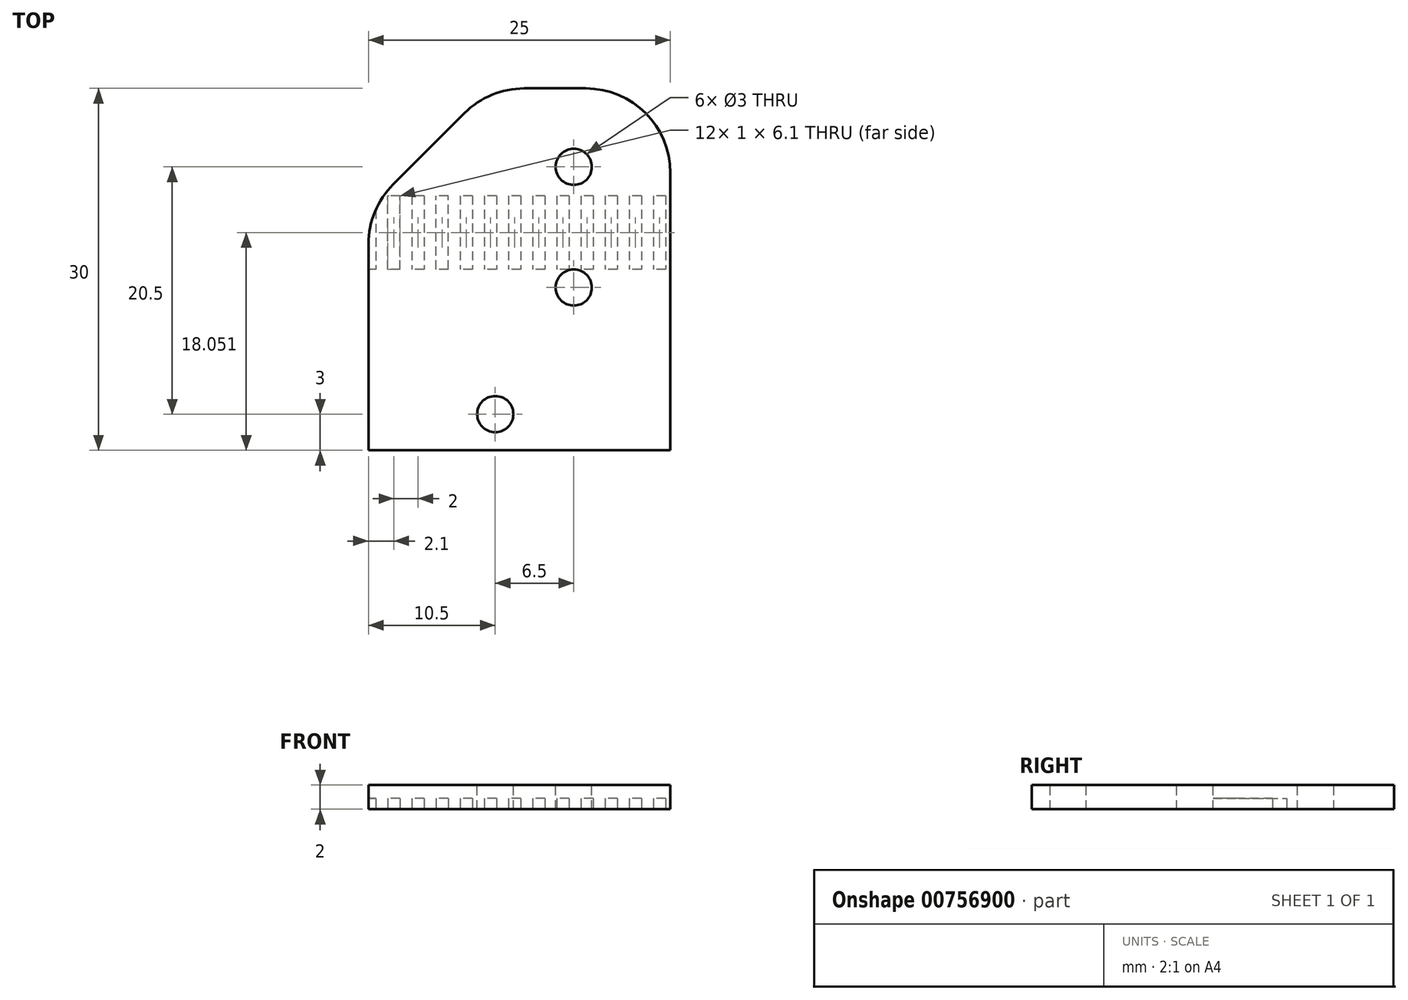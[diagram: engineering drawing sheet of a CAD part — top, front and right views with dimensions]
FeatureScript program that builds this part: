
annotation { "Feature Type Name" : "Feature", "Feature Type Description" : "" }
export const myFeature = defineFeature(function(context is Context, id is Id, definition is map)
    precondition{}
    {
        {
            var Q0;
            Q0=qCreatedBy(makeId("Top.planeOp"),FACE);
            var sketch = newSketch(context, id + "F0", { "sketchPlane" : qUnion([Q0])});
            skLineSegment(sketch, "E0.bottom", {"start": v(12.5, -15) * mm, "end": v(-12.5, -15) * mm});
            skLineSegment(sketch, "E0.top", {"start": v(12.5, 15) * mm, "end": v(-12.5, 15) * mm});
            skLineSegment(sketch, "E0.left", {"start": v(12.5, -15) * mm, "end": v(12.5, 15) * mm});
            skLineSegment(sketch, "E0.right", {"start": v(-12.5, -15) * mm, "end": v(-12.5, 15) * mm});
            skPoint(sketch, "E0.middle", {"position": v(0, 0) * mm});
            skSolve(sketch);
        }
        {
            var Q0;
            Q0=makeQuery(id+"F0.imprint","IMPRINT",FACE,{"disambiguationData":[TD([[makeQuery(id+"F0.imprint","IMPRINT",EDGE,{"derivedFrom":sQuery(id+"F0.wireOp",EDGE,"E0.bottom")}),-1.0]])]});
            extrude(context, id + "F1", {"entities" : qUnion([Q0]), "depth" : 2 * mm, "offsetDistance" : 25 * mm});
        }
        {
            var Q0;
            Q0=makeQuery(id+"F1.opExtrude","CAP_FACE",FACE,{"disambiguationData":[OSD([sQuery(id+"F0.wireOp",EDGE,"E0.bottom"),sQuery(id+"F0.wireOp",EDGE,"E0.top"),sQuery(id+"F0.wireOp",EDGE,"E0.left"),sQuery(id+"F0.wireOp",EDGE,"E0.right")])],"isStart":false});
            var sketch = newSketch(context, id + "F2", { "sketchPlane" : qUnion([Q0])});
            skCircle(sketch, "E1", {"center": v(-2, -12) * mm, "radius": 1.5 * mm});
            skPoint(sketch, "E1.centerSnap0", {"position": v(0, -15) * mm});
            skCircle(sketch, "E2", {"center": v(4.5, -1.5) * mm, "radius": 1.5 * mm});
            skCircle(sketch, "E3", {"center": v(4.5, 8.5) * mm, "radius": 1.5 * mm});
            skSolve(sketch);
        }
        {
            var Q0;
            Q0=qSketchRegion(id+"F2",true);
            extrude(context, id + "F3", {"entities" : qUnion([Q0]), "operationType" : NewBodyOperationType.REMOVE, "endBound" : BoundingType.THROUGH_ALL, "oppositeDirection" : true, "depth" : 25 * mm, "offsetDistance" : 25 * mm});
        }
        {
            var Q0;
            {var subQ0=sQuery(id+"F0.wireOp",EDGE,"E0.right");var subQ1=sQuery(id+"F0.wireOp",EDGE,"E0.left");var subQ2=sQuery(id+"F0.wireOp",EDGE,"E0.bottom");Q0=makeQuery(id+"F5.boolean.opBoolean","SPLIT",FACE,{"disambiguationData":[TD([makeQuery(id+"F1.opExtrude","SWEPT_FACE",FACE,{"disambiguationData":[OSD([subQ2])]})])],"derivedFrom":makeQuery(id+"F1.opExtrude","CAP_FACE",FACE,{"disambiguationData":[OSD([subQ2,sQuery(id+"F0.wireOp",EDGE,"E0.top"),subQ1,subQ0])],"isStart":true})});}
            var sketch = newSketch(context, id + "F4", { "sketchPlane" : qUnion([Q0])});
            skLineSegment(sketch, "E4.bottom", {"start": v(12.1, -6.1) * mm, "end": v(11.1, -6.1) * mm});
            skLineSegment(sketch, "E4.top", {"start": v(12.1, 0) * mm, "end": v(11.1, 0) * mm});
            skLineSegment(sketch, "E4.left", {"start": v(12.1, -6.1) * mm, "end": v(12.1, 0) * mm});
            skLineSegment(sketch, "E4.right", {"start": v(11.1, -6.1) * mm, "end": v(11.1, 0) * mm});
            skPoint(sketch, "E4.middle", {"position": v(11.6, -3.05) * mm});
            skLineSegment(sketch, "E5.bottom", {"start": v(10.1, -6.1) * mm, "end": v(9.1, -6.1) * mm});
            skLineSegment(sketch, "E5.top", {"start": v(10.1, 0) * mm, "end": v(9.1, 0) * mm});
            skLineSegment(sketch, "E5.left", {"start": v(10.1, -6.1) * mm, "end": v(10.1, 0) * mm});
            skLineSegment(sketch, "E5.right", {"start": v(9.1, -6.1) * mm, "end": v(9.1, 0) * mm});
            skPoint(sketch, "E5.middle", {"position": v(9.6, -3.05) * mm});
            skLineSegment(sketch, "E6.bottom", {"start": v(8.1, -6.1) * mm, "end": v(7.1, -6.1) * mm});
            skLineSegment(sketch, "E6.top", {"start": v(8.1, 0) * mm, "end": v(7.1, 0) * mm});
            skLineSegment(sketch, "E6.left", {"start": v(8.1, -6.1) * mm, "end": v(8.1, 0) * mm});
            skLineSegment(sketch, "E6.right", {"start": v(7.1, -6.1) * mm, "end": v(7.1, 0) * mm});
            skPoint(sketch, "E6.middle", {"position": v(7.6, -3.05) * mm});
            skLineSegment(sketch, "E7.bottom", {"start": v(6.1, -6.1) * mm, "end": v(5.1, -6.1) * mm});
            skLineSegment(sketch, "E7.top", {"start": v(6.1, 0) * mm, "end": v(5.1, 0) * mm});
            skLineSegment(sketch, "E7.left", {"start": v(6.1, -6.1) * mm, "end": v(6.1, 0) * mm});
            skLineSegment(sketch, "E7.right", {"start": v(5.1, -6.1) * mm, "end": v(5.1, 0) * mm});
            skPoint(sketch, "E7.middle", {"position": v(5.6, -3.05) * mm});
            skLineSegment(sketch, "E8.bottom", {"start": v(4.1, -6.1) * mm, "end": v(3.1, -6.1) * mm});
            skLineSegment(sketch, "E8.top", {"start": v(4.1, 0) * mm, "end": v(3.1, 0) * mm});
            skLineSegment(sketch, "E8.left", {"start": v(4.1, -6.1) * mm, "end": v(4.1, 0) * mm});
            skLineSegment(sketch, "E8.right", {"start": v(3.1, -6.1) * mm, "end": v(3.1, 0) * mm});
            skPoint(sketch, "E8.middle", {"position": v(3.6, -3.05) * mm});
            skLineSegment(sketch, "E9.bottom", {"start": v(2.1, -6.1) * mm, "end": v(1.1, -6.1) * mm});
            skLineSegment(sketch, "E9.top", {"start": v(2.1, 0) * mm, "end": v(1.1, 0) * mm});
            skLineSegment(sketch, "E9.left", {"start": v(2.1, -6.1) * mm, "end": v(2.1, 0) * mm});
            skLineSegment(sketch, "E9.right", {"start": v(1.1, -6.1) * mm, "end": v(1.1, 0) * mm});
            skPoint(sketch, "E9.middle", {"position": v(1.6, -3.05) * mm});
            skLineSegment(sketch, "E10.bottom", {"start": v(0.1, -6.1) * mm, "end": v(-0.9, -6.1) * mm});
            skLineSegment(sketch, "E10.top", {"start": v(0.1, 0) * mm, "end": v(-0.9, 0) * mm});
            skLineSegment(sketch, "E10.left", {"start": v(0.1, -6.1) * mm, "end": v(0.1, 0) * mm});
            skLineSegment(sketch, "E10.right", {"start": v(-0.9, -6.1) * mm, "end": v(-0.9, 0) * mm});
            skPoint(sketch, "E10.middle", {"position": v(-0.4, -3.05) * mm});
            skLineSegment(sketch, "E11", {"start": v(-12.5, -6.1) * mm, "end": v(12.5, -6.1) * mm, "construction": true});
            skLineSegment(sketch, "E12", {"start": v(12.5, 0) * mm, "end": v(-12.5, 0) * mm, "construction": true});
            skLineSegment(sketch, "E13.bottom", {"start": v(-1.9, -6.1) * mm, "end": v(-2.9, -6.1) * mm});
            skLineSegment(sketch, "E13.top", {"start": v(-1.9, 0) * mm, "end": v(-2.9, 0) * mm});
            skLineSegment(sketch, "E13.left", {"start": v(-1.9, -6.1) * mm, "end": v(-1.9, 0) * mm});
            skLineSegment(sketch, "E13.right", {"start": v(-2.9, -6.1) * mm, "end": v(-2.9, 0) * mm});
            skLineSegment(sketch, "E14.bottom", {"start": v(-3.9, -6.1) * mm, "end": v(-4.9, -6.1) * mm});
            skLineSegment(sketch, "E14.top", {"start": v(-3.9, 0) * mm, "end": v(-4.9, 0) * mm});
            skLineSegment(sketch, "E14.left", {"start": v(-3.9, -6.1) * mm, "end": v(-3.9, 0) * mm});
            skLineSegment(sketch, "E14.right", {"start": v(-4.9, -6.1) * mm, "end": v(-4.9, 0) * mm});
            skLineSegment(sketch, "E15.bottom", {"start": v(-5.9, 0) * mm, "end": v(-6.9, 0) * mm});
            skLineSegment(sketch, "E15.top", {"start": v(-5.9, -6.1) * mm, "end": v(-6.9, -6.1) * mm});
            skLineSegment(sketch, "E15.left", {"start": v(-5.9, 0) * mm, "end": v(-5.9, -6.1) * mm});
            skLineSegment(sketch, "E15.right", {"start": v(-6.9, 0) * mm, "end": v(-6.9, -6.1) * mm});
            skLineSegment(sketch, "E16.bottom", {"start": v(-7.9, -6.1) * mm, "end": v(-8.9, -6.1) * mm});
            skLineSegment(sketch, "E16.top", {"start": v(-7.9, 0) * mm, "end": v(-8.9, 0) * mm});
            skLineSegment(sketch, "E16.left", {"start": v(-7.9, -6.1) * mm, "end": v(-7.9, 0) * mm});
            skLineSegment(sketch, "E16.right", {"start": v(-8.9, -6.1) * mm, "end": v(-8.9, 0) * mm});
            skLineSegment(sketch, "E17.bottom", {"start": v(-9.9, 0) * mm, "end": v(-10.9, 0) * mm});
            skLineSegment(sketch, "E17.top", {"start": v(-9.9, -6.1) * mm, "end": v(-10.9, -6.1) * mm});
            skLineSegment(sketch, "E17.left", {"start": v(-9.9, 0) * mm, "end": v(-9.9, -6.1) * mm});
            skLineSegment(sketch, "E17.right", {"start": v(-10.9, 0) * mm, "end": v(-10.9, -6.1) * mm});
            skLineSegment(sketch, "E18.bottom", {"start": v(-11.9, -6.1) * mm, "end": v(-12.9, -6.1) * mm});
            skLineSegment(sketch, "E18.top", {"start": v(-11.9, 0) * mm, "end": v(-12.9, 0) * mm});
            skLineSegment(sketch, "E18.left", {"start": v(-11.9, -6.1) * mm, "end": v(-11.9, 0) * mm});
            skLineSegment(sketch, "E18.right", {"start": v(-12.9, -6.1) * mm, "end": v(-12.9, 0) * mm});
            skSolve(sketch);
        }
        {
            var Q0;
            Q0 = qSketchRegion(id + "F4", true);
            extrude(context, id + "F5", {"entities" : qUnion([Q0]), "operationType" : NewBodyOperationType.REMOVE, "oppositeDirection" : true, "depth" : 0.9 * mm, "offsetDistance" : 25 * mm});
        }
        {
            var Q0;
            Q0=makeQuery(id+"F1.opExtrude","SWEPT_EDGE",EDGE,{"disambiguationData":[OSD([sQuery(id+"F0.wireOp",EDGE,"E0.top"),sQuery(id+"F0.wireOp",EDGE,"E0.right")])]});
            chamfer(context, id + "F6", {"entities" : qUnion([Q0]), "width" : 10 * mm, "tangentPropagation" : true});
        }
        {
            var Q0;
            {var subQ0=sQuery(id+"F0.wireOp",EDGE,"E0.right");Q0=makeQuery(id+"F6.opChamfer","BLEND_EDGE",EDGE,{"blendedFrom":[makeQuery(id+"F1.opExtrude","SWEPT_EDGE",EDGE,{"disambiguationData":[OSD([sQuery(id+"F0.wireOp",EDGE,"E0.top"),subQ0])]}),makeQuery(id+"F1.opExtrude","SWEPT_FACE",FACE,{"disambiguationData":[OSD([subQ0])]})],"blendedInto":[makeQuery(id+"F1.opExtrude","SWEPT_FACE",FACE,{"disambiguationData":[OSD([subQ0])]})]});}
            var Q1;
            {var subQ0=sQuery(id+"F0.wireOp",EDGE,"E0.top");Q1=makeQuery(id+"F6.opChamfer","BLEND_EDGE",EDGE,{"blendedFrom":[makeQuery(id+"F1.opExtrude","SWEPT_EDGE",EDGE,{"disambiguationData":[OSD([subQ0,sQuery(id+"F0.wireOp",EDGE,"E0.right")])]}),makeQuery(id+"F1.opExtrude","SWEPT_FACE",FACE,{"disambiguationData":[OSD([subQ0])]})],"blendedInto":[makeQuery(id+"F1.opExtrude","SWEPT_FACE",FACE,{"disambiguationData":[OSD([subQ0])]})]});}
            var Q2;
            Q2=makeQuery(id+"F1.opExtrude","SWEPT_EDGE",EDGE,{"disambiguationData":[OSD([sQuery(id+"F0.wireOp",EDGE,"E0.top"),sQuery(id+"F0.wireOp",EDGE,"E0.left")])]});
            fillet(context, id + "F7", {"entities" : qUnion([Q0, Q1, Q2]), "radius" : 7 * mm, "tangentPropagation" : true, "allowEdgeOverflow" : false});
        }
    });
